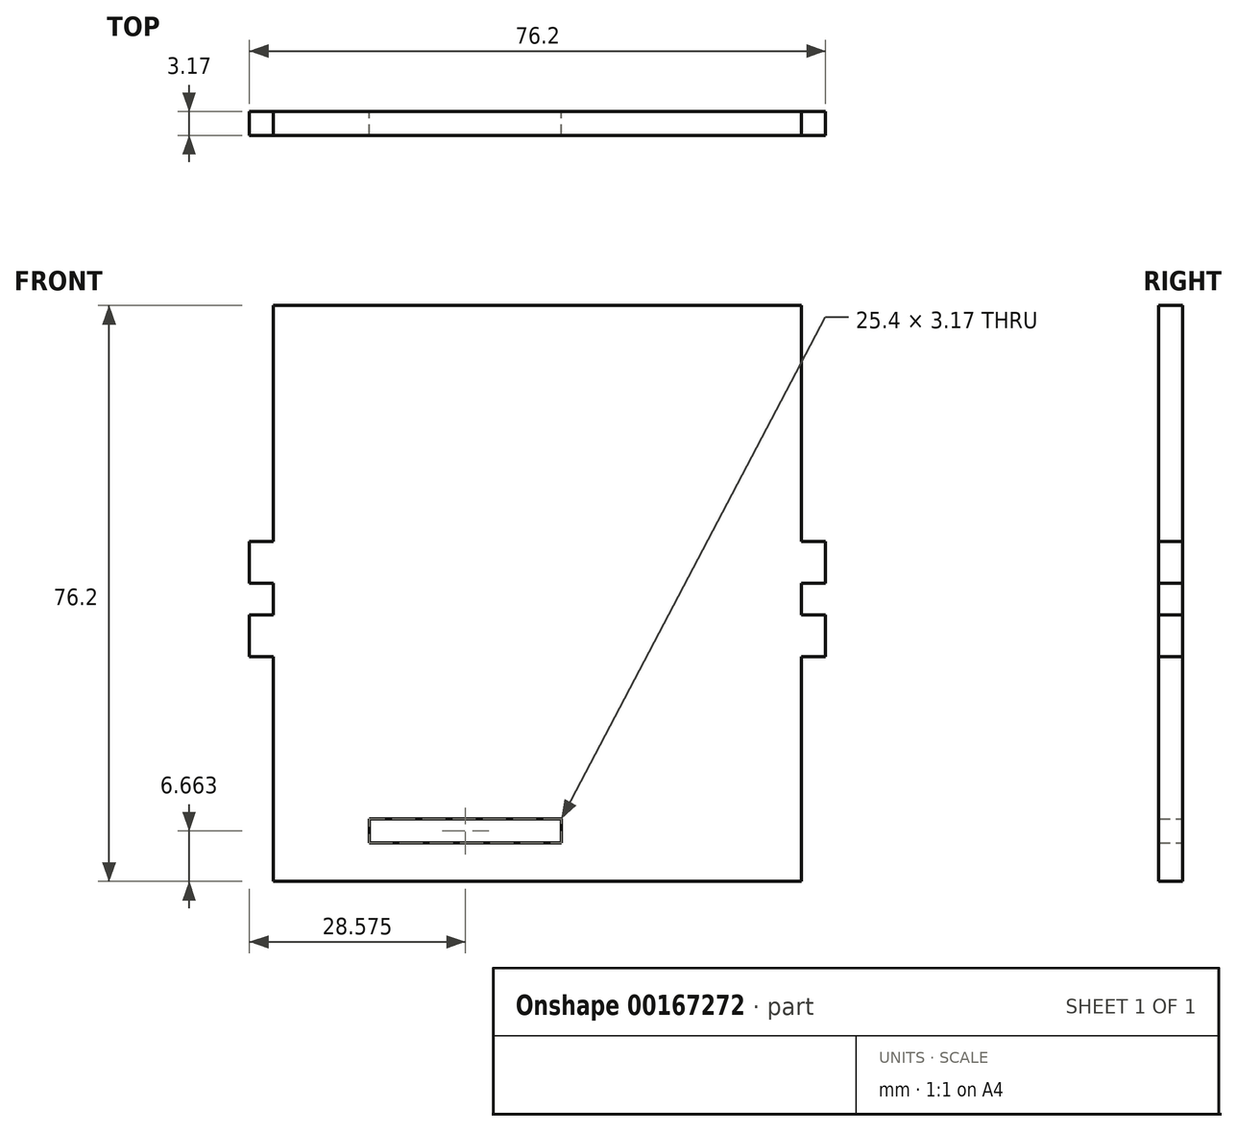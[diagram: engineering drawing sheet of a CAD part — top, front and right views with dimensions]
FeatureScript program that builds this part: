
annotation { "Feature Type Name" : "Feature", "Feature Type Description" : "" }
export const myFeature = defineFeature(function(context is Context, id is Id, definition is map)
    precondition{}
    {
        {
            var Q0;
            Q0=qCreatedBy(makeId("Front.planeOp"),FACE);
            var sketch = newSketch(context, id + "F0", { "sketchPlane" : qUnion([Q0])});
            skLineSegment(sketch, "E0.bottom", {"start": v(34.92, -37.38) * mm, "end": v(-34.92, -37.38) * mm});
            skLineSegment(sketch, "E0.top", {"start": v(34.92, 38.82) * mm, "end": v(-34.93, 38.82) * mm});
            skLineSegment(sketch, "E0.left", {"start": v(38.1, -7.62) * mm, "end": v(38.1, -2.08) * mm});
            skLineSegment(sketch, "E0.right", {"start": v(-38.1, -7.62) * mm, "end": v(-38.1, -2.08) * mm});
            skPoint(sketch, "E0.middle", {"position": v(0, 0) * mm});
            skLineSegment(sketch, "E1.bottom", {"start": v(-34.92, -7.62) * mm, "end": v(-38.1, -7.62) * mm});
            skLineSegment(sketch, "E1.top", {"start": v(-34.92, 7.62) * mm, "end": v(-38.1, 7.62) * mm});
            skLineSegment(sketch, "E1.left", {"start": v(-34.93, -2.08) * mm, "end": v(-34.93, 2.08) * mm});
            skLineSegment(sketch, "E2.MirrorCS", {"start": v(34.92, -7.62) * mm, "end": v(38.1, -7.62) * mm});
            skLineSegment(sketch, "E3.MirrorCS", {"start": v(34.92, 7.62) * mm, "end": v(38.1, 7.62) * mm});
            skLineSegment(sketch, "E4.MirrorCS", {"start": v(34.92, -2.08) * mm, "end": v(34.92, 2.08) * mm});
            skLineSegment(sketch, "E5", {"start": v(-34.93, 7.62) * mm, "end": v(-34.93, 38.82) * mm});
            skLineSegment(sketch, "E6", {"start": v(-34.92, -7.62) * mm, "end": v(-34.92, -37.38) * mm});
            skLineSegment(sketch, "E7.bottom", {"start": v(-34.92, -2.08) * mm, "end": v(-38.18, -2.08) * mm});
            skLineSegment(sketch, "E7.top", {"start": v(-34.93, 2.08) * mm, "end": v(-38.18, 2.08) * mm});
            skLineSegment(sketch, "E8.trimOffspring", {"start": v(-38.1, 2.08) * mm, "end": v(-38.1, 7.62) * mm});
            skPoint(sketch, "E9.MirrorCS.start.orphan", {"position": v(-34.93, -7.62) * mm});
            skLineSegment(sketch, "E10", {"start": v(34.92, 7.62) * mm, "end": v(34.92, 38.82) * mm});
            skLineSegment(sketch, "E11", {"start": v(34.92, -7.62) * mm, "end": v(34.92, -37.38) * mm});
            skLineSegment(sketch, "E12.MirrorCS", {"start": v(34.93, -2.08) * mm, "end": v(34.93, 2.08) * mm});
            skLineSegment(sketch, "E13", {"start": v(34.93, 2.08) * mm, "end": v(38.1, 2.08) * mm});
            skLineSegment(sketch, "E14", {"start": v(34.93, -2.08) * mm, "end": v(38.1, -2.08) * mm});
            skLineSegment(sketch, "E15.trimOffspring", {"start": v(38.1, 2.08) * mm, "end": v(38.1, 7.62) * mm});
            skLineSegment(sketch, "E16.bottom", {"start": v(-22.22, -32.3) * mm, "end": v(3.18, -32.3) * mm});
            skLineSegment(sketch, "E16.top", {"start": v(-22.22, -29.13) * mm, "end": v(3.18, -29.13) * mm});
            skLineSegment(sketch, "E16.left", {"start": v(-22.22, -32.3) * mm, "end": v(-22.22, -29.13) * mm});
            skLineSegment(sketch, "E16.right", {"start": v(3.18, -32.3) * mm, "end": v(3.18, -29.13) * mm});
            skSolve(sketch);
        }
        {
            var Q0;
            Q0=makeQuery(id+"F0.imprint","IMPRINT",FACE,{"disambiguationData":[TD([[makeQuery(id+"F0.imprint","IMPRINT",EDGE,{"derivedFrom":sQuery(id+"F0.wireOp",EDGE,"E0.bottom")}),-1.0]])]});
            extrude(context, id + "F1", {"entities" : qUnion([Q0]), "depth" : 3.17 * mm});
        }
    });
